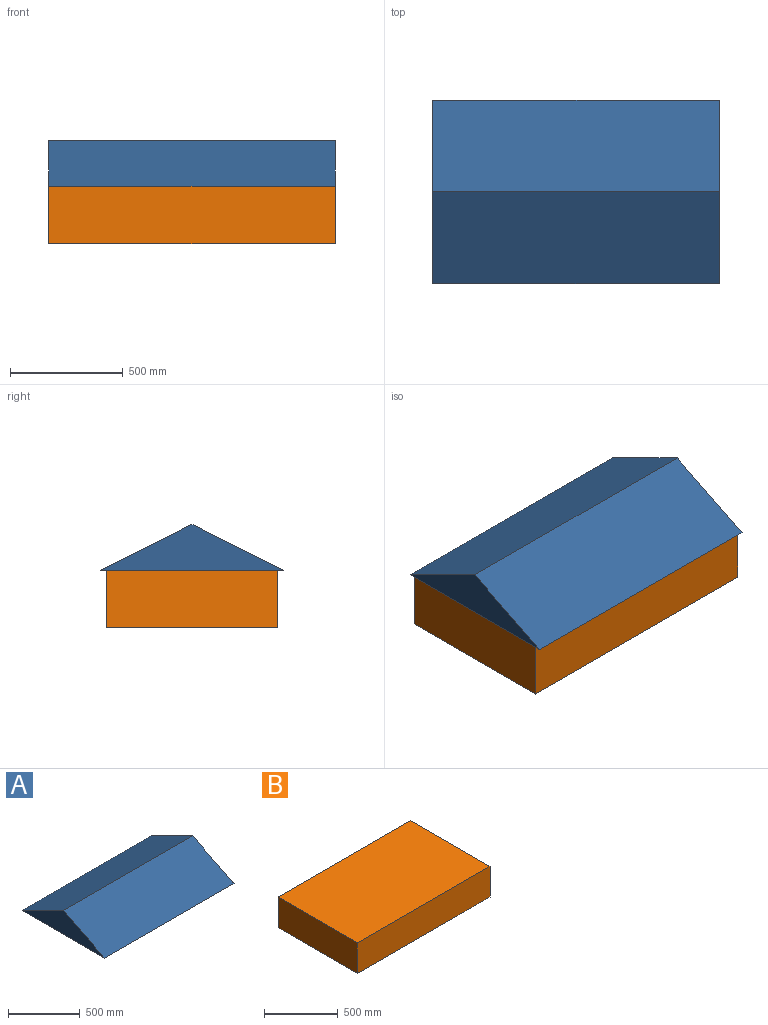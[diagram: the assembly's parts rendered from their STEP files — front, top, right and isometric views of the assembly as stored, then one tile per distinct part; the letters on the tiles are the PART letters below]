
ASSEMBLY  parts=2 mates=1
PART A: 5 faces, bbox 1270x812.8x203.2 mm
  f0: plane 1270x812.8mm, normal (0,0,-1), area 1032256mm2, adj f1,f2,f3,f4
  f1: plane 1270x406.4mm, normal (0,0.45,0.89), area 577048.6mm2, adj f0,f2,f3,f4
  f2: plane 1270x406.4mm, normal (0,-0.45,0.89), area 577048.6mm2, adj f0,f1,f3,f4
  f3: plane 812.8x203.2mm, normal (1,0,0), area 82580.5mm2, adj f0,f1,f2
  f4: plane 812.8x203.2mm, normal (-1,0,0), area 82580.5mm2, adj f0,f1,f2
PART B: 6 faces, bbox 1270x762x254 mm
  f0: plane 1270x254mm, normal (0,-1,0), area 322580mm2, adj f1,f3,f4,f5
  f1: plane 762x254mm, normal (1,0,0), area 193548mm2, adj f0,f2,f4,f5
  f2: plane 1270x254mm, normal (0,1,0), area 322580mm2, adj f1,f3,f4,f5
  f3: plane 762x254mm, normal (-1,0,0), area 193548mm2, adj f0,f2,f4,f5
  f4: plane 1270x762mm, normal (0,0,1), area 967740mm2, adj f0,f1,f2,f3
  f5: plane 1270x762mm, normal (0,0,-1), area 967740mm2, adj f0,f1,f2,f3
PLACE A t=(-499.93,-23.68,164.33)mm
PLACE B t=(770.07,-404.68,0.98)mm fixed
MATE fastened B.f4 <-> A.f0  axis (0,0,1) through (135.07,-23.68,254.98)mm
